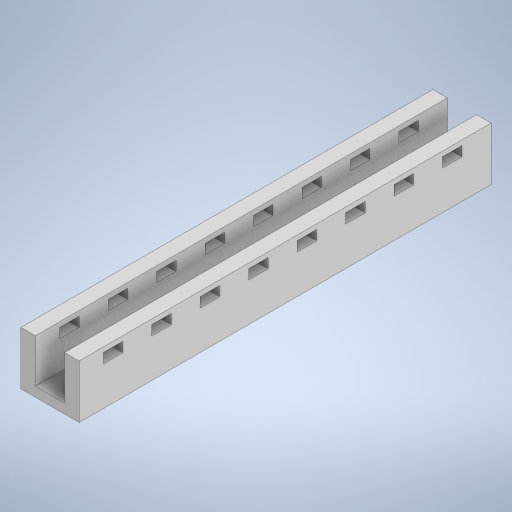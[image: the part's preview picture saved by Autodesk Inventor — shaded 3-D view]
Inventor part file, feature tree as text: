
AUTODESK INVENTOR PART (.ipt)
format: ipt  version: 2024.2 (Build 282272000, 272)  size: 316,928 bytes
history: native  units: mm
features: extrude x3, sketch x3, chamfer x2, other x1, projected_geometry x1
ambient origin geometry x8: Origin, YZ Plane, XZ Plane, XY Plane, X Axis, Y Axis, Z Axis, Center Point
bodies: Body1 (feature_tree)
feature tree (10):
  other  "Твердое тело1"
  extrude  "Выдавливание1"  Depth=4.0mm
  extrude  "Выдавливание2"  Depth=22.0mm
  chamfer  "Фаска1"  Distance=22.0mm
  chamfer  "Фаска2"  Distance=85.0mm
  extrude  "Выдавливание3"  Depth=12.0mm
  sketch  "Эскиз1"
  sketch  "Эскиз2"
  projected_geometry  "Спроецированная петля1"
  sketch  "Эскиз3"
